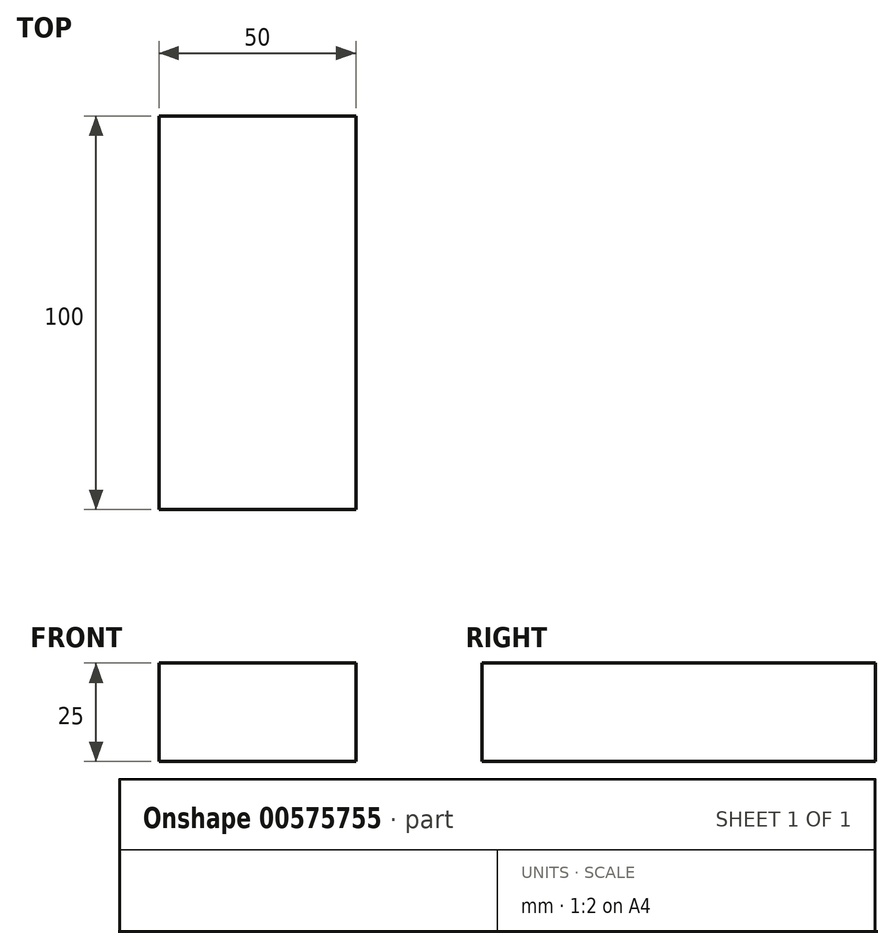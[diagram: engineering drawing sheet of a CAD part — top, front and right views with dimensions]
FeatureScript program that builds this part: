
annotation { "Feature Type Name" : "Feature", "Feature Type Description" : "" }
export const myFeature = defineFeature(function(context is Context, id is Id, definition is map)
    precondition{}
    {
        {
            var Q0;
            Q0=qCreatedBy(makeId("Front.planeOp"),FACE);
            var sketch = newSketch(context, id + "F0", { "sketchPlane" : qUnion([Q0])});
            skLineSegment(sketch, "E0.bottom", {"start": v(-50, 25) * mm, "end": v(0, 25) * mm});
            skLineSegment(sketch, "E0.top", {"start": v(-50, 0) * mm, "end": v(0, 0) * mm});
            skLineSegment(sketch, "E0.left", {"start": v(-50, 25) * mm, "end": v(-50, 0) * mm});
            skLineSegment(sketch, "E0.right", {"start": v(0, 25) * mm, "end": v(0, 0) * mm});
            skSolve(sketch);
        }
        {
            var Q0;
            Q0 = qSketchRegion(id + "F0", true);
            extrude(context, id + "F1", {"entities" : qUnion([Q0]), "depth" : 75 * mm, "offsetDistance" : 25.4 * mm});
        }
        {
            var Q0;
            Q0=makeQuery(id+"F1.opExtrude","CAP_FACE",FACE,{"disambiguationData":[OSD([sQuery(id+"F0.wireOp",EDGE,"E0.bottom"),sQuery(id+"F0.wireOp",EDGE,"E0.top"),sQuery(id+"F0.wireOp",EDGE,"E0.left"),sQuery(id+"F0.wireOp",EDGE,"E0.right")])],"isStart":false});
            extrude(context, id + "F2", {"entities" : qUnion([Q0]), "operationType" : NewBodyOperationType.ADD, "depth" : 25 * mm, "offsetDistance" : 25 * mm});
        }
    });
